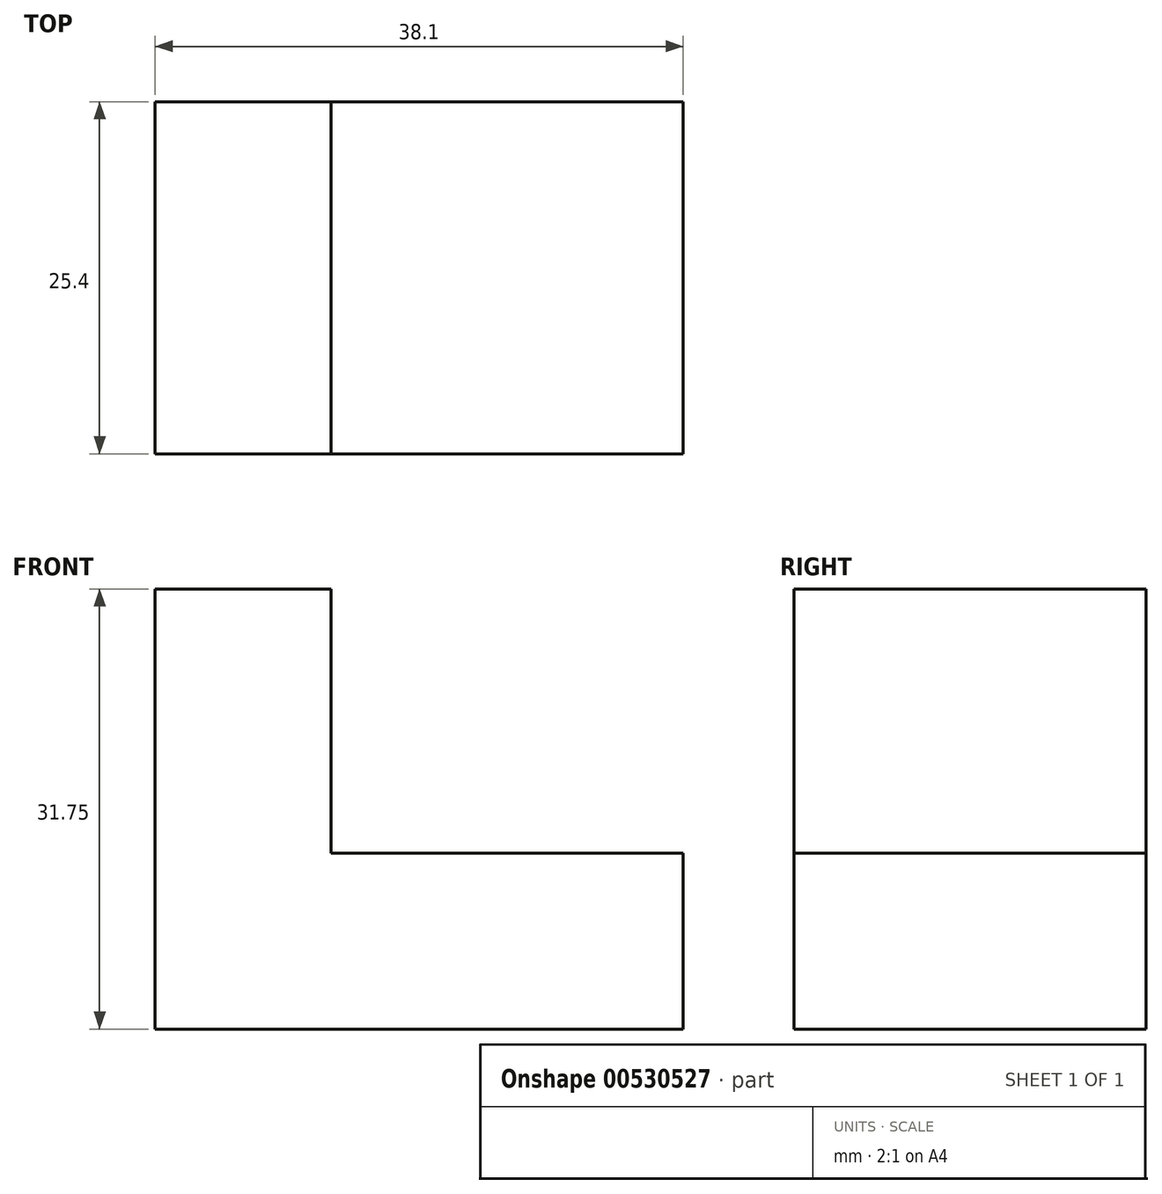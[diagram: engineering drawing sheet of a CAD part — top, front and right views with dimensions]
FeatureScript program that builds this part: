
annotation { "Feature Type Name" : "Feature", "Feature Type Description" : "" }
export const myFeature = defineFeature(function(context is Context, id is Id, definition is map)
    precondition{}
    {
        {
            var Q0;
            Q0=qCreatedBy(makeId("Front.planeOp"),FACE);
            var sketch = newSketch(context, id + "F0", { "sketchPlane" : qUnion([Q0])});
            skLineSegment(sketch, "E0", {"start": v(-88.9, 31.75) * mm, "end": v(-88.9, 0) * mm});
            skLineSegment(sketch, "E1", {"start": v(-88.9, 0) * mm, "end": v(-50.8, 0) * mm});
            skLineSegment(sketch, "E2", {"start": v(-50.8, 0) * mm, "end": v(-50.8, 12.7) * mm});
            skLineSegment(sketch, "E3", {"start": v(-50.8, 12.7) * mm, "end": v(-76.2, 12.7) * mm});
            skLineSegment(sketch, "E4", {"start": v(-76.2, 12.7) * mm, "end": v(-76.2, 31.75) * mm});
            skLineSegment(sketch, "E5", {"start": v(-88.9, 31.75) * mm, "end": v(-76.2, 31.75) * mm});
            skSolve(sketch);
        }
        {
            var Q0;
            Q0 = qSketchRegion(id + "F0", true);
            extrude(context, id + "F1", {"entities" : qUnion([Q0]), "depth" : 25.4 * mm, "offsetDistance" : 25.4 * mm});
        }
    });
